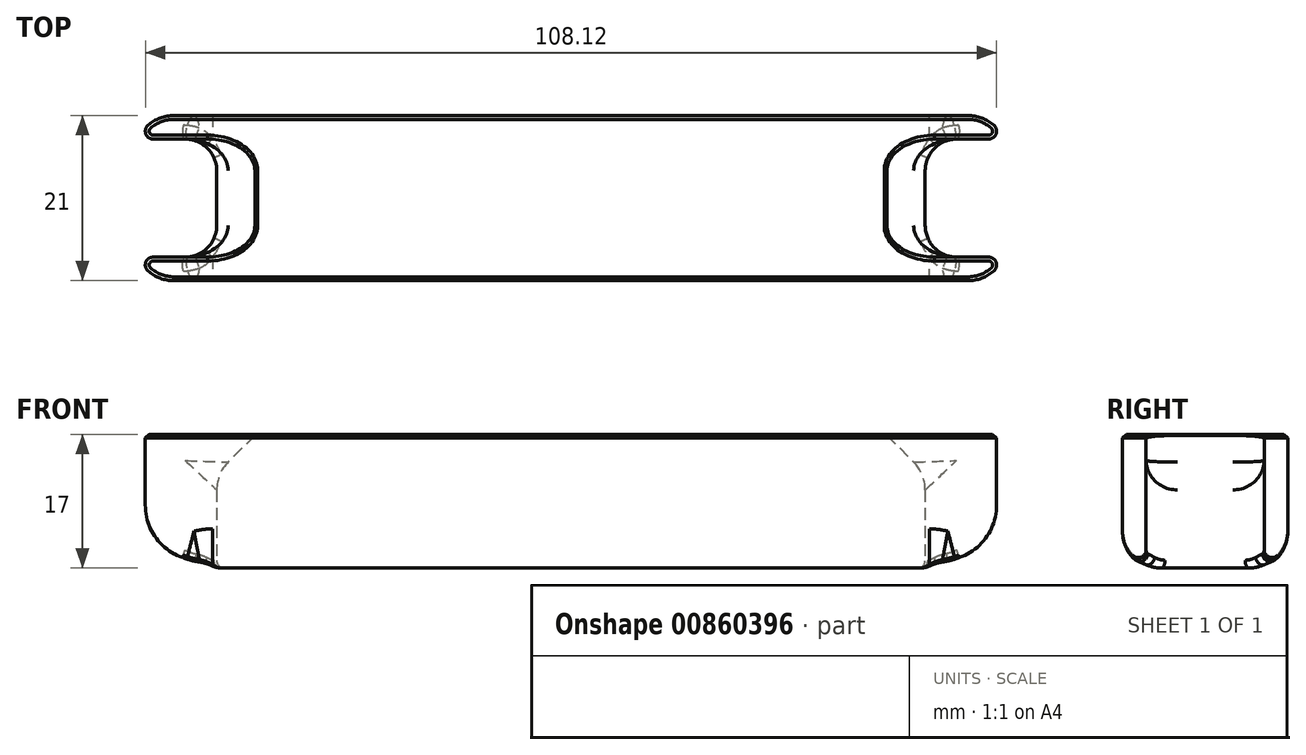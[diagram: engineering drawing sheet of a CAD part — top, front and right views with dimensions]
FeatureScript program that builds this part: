
annotation { "Feature Type Name" : "Feature", "Feature Type Description" : "" }
export const myFeature = defineFeature(function(context is Context, id is Id, definition is map)
    precondition{}
    {
        {
            var Q0;
            Q0=qCreatedBy(makeId("Top.planeOp"),FACE);
            var sketch = newSketch(context, id + "F0", { "sketchPlane" : qUnion([Q0])});
            skLineSegment(sketch, "E0.bottom", {"start": v(55, -10.5) * mm, "end": v(-55, -10.5) * mm});
            skLineSegment(sketch, "E0.top", {"start": v(55, 10.5) * mm, "end": v(-55, 10.5) * mm});
            skLineSegment(sketch, "E0.left", {"start": v(55, -10.5) * mm, "end": v(55, 10.5) * mm});
            skLineSegment(sketch, "E0.right", {"start": v(-55, -10.5) * mm, "end": v(-55, 10.5) * mm});
            skPoint(sketch, "E0.middle", {"position": v(0, 0) * mm});
            skLineSegment(sketch, "E1.bottom", {"start": v(-55, 7.5) * mm, "end": v(-45, 7.5) * mm});
            skLineSegment(sketch, "E1.top", {"start": v(-55, -7.5) * mm, "end": v(-45, -7.5) * mm});
            skLineSegment(sketch, "E1.left", {"start": v(-55, 7.5) * mm, "end": v(-55, -7.5) * mm});
            skLineSegment(sketch, "E1.right", {"start": v(-45, 7.5) * mm, "end": v(-45, -7.5) * mm});
            skLineSegment(sketch, "E2.bottom", {"start": v(55, 7.5) * mm, "end": v(45, 7.5) * mm});
            skLineSegment(sketch, "E2.top", {"start": v(55, -7.5) * mm, "end": v(45, -7.5) * mm});
            skLineSegment(sketch, "E2.left", {"start": v(55, 7.5) * mm, "end": v(55, -7.5) * mm});
            skLineSegment(sketch, "E2.right", {"start": v(45, 7.5) * mm, "end": v(45, -7.5) * mm});
            skSolve(sketch);
        }
        {
            var Q0;
            {var subQ6=sQuery(id+"F0.wireOp",EDGE,"E0.bottom");Q0=makeQuery(id+"F0.imprint","IMPRINT",FACE,{"disambiguationData":[TD([[makeQuery(id+"F0.imprint","IMPRINT",EDGE,{"derivedFrom":subQ6}),-1.0]])]});}
            extrude(context, id + "F1", {"entities" : qUnion([Q0]), "depth" : 17 * mm, "offsetDistance" : 25 * mm});
        }
        {
            var Q0;
            Q0=makeQuery(id+"F1.opExtrude","CAP_EDGE",EDGE,{"disambiguationData":[OSD([sQuery(id+"F0.wireOp",EDGE,"E1.right")])],"isStart":false});
            var Q1;
            Q1=makeQuery(id+"F1.opExtrude","CAP_EDGE",EDGE,{"disambiguationData":[OSD([sQuery(id+"F0.wireOp",EDGE,"E2.right")])],"isStart":false});
            chamfer(context, id + "F2", {"entities" : qUnion([Q0, Q1]), "width" : 5 * mm, "tangentPropagation" : true});
        }
        {
            var Q0;
            Q0=makeQuery(id+"F1.opExtrude","SWEPT_EDGE",EDGE,{"disambiguationData":[OSD([sQuery(id+"F0.wireOp",EDGE,"E2.bottom"),sQuery(id+"F0.wireOp",EDGE,"E2.right")])]});
            var Q1;
            Q1=makeQuery(id+"F1.opExtrude","SWEPT_EDGE",EDGE,{"disambiguationData":[OSD([sQuery(id+"F0.wireOp",EDGE,"E2.top"),sQuery(id+"F0.wireOp",EDGE,"E2.right")])]});
            var Q2;
            Q2=makeQuery(id+"F1.opExtrude","SWEPT_EDGE",EDGE,{"disambiguationData":[OSD([sQuery(id+"F0.wireOp",EDGE,"E1.top"),sQuery(id+"F0.wireOp",EDGE,"E1.right")])]});
            var Q3;
            Q3=makeQuery(id+"F1.opExtrude","SWEPT_EDGE",EDGE,{"disambiguationData":[OSD([sQuery(id+"F0.wireOp",EDGE,"E1.bottom"),sQuery(id+"F0.wireOp",EDGE,"E1.right")])]});
            var Q4;
            Q4=makeQuery(id+"F2.opChamfer","BLEND_EDGE",EDGE,{"blendedFrom":[makeQuery(id+"F1.opExtrude","CAP_EDGE",EDGE,{"disambiguationData":[OSD([sQuery(id+"F0.wireOp",EDGE,"E1.right")])],"isStart":false}),makeQuery(id+"F1.opExtrude","SWEPT_FACE",FACE,{"disambiguationData":[OSD([sQuery(id+"F0.wireOp",EDGE,"E1.top")])]})],"blendedInto":[makeQuery(id+"F1.opExtrude","SWEPT_FACE",FACE,{"disambiguationData":[OSD([sQuery(id+"F0.wireOp",EDGE,"E1.top")])]})]});
            var Q5;
            Q5=makeQuery(id+"F2.opChamfer","BLEND_EDGE",EDGE,{"blendedFrom":[makeQuery(id+"F1.opExtrude","CAP_EDGE",EDGE,{"disambiguationData":[OSD([sQuery(id+"F0.wireOp",EDGE,"E1.right")])],"isStart":false}),makeQuery(id+"F1.opExtrude","SWEPT_FACE",FACE,{"disambiguationData":[OSD([sQuery(id+"F0.wireOp",EDGE,"E1.bottom")])]})],"blendedInto":[makeQuery(id+"F1.opExtrude","SWEPT_FACE",FACE,{"disambiguationData":[OSD([sQuery(id+"F0.wireOp",EDGE,"E1.bottom")])]})]});
            var Q6;
            Q6=makeQuery(id+"F2.opChamfer","BLEND_EDGE",EDGE,{"blendedFrom":[makeQuery(id+"F1.opExtrude","CAP_EDGE",EDGE,{"disambiguationData":[OSD([sQuery(id+"F0.wireOp",EDGE,"E2.right")])],"isStart":false}),makeQuery(id+"F1.opExtrude","SWEPT_FACE",FACE,{"disambiguationData":[OSD([sQuery(id+"F0.wireOp",EDGE,"E2.bottom")])]})],"blendedInto":[makeQuery(id+"F1.opExtrude","SWEPT_FACE",FACE,{"disambiguationData":[OSD([sQuery(id+"F0.wireOp",EDGE,"E2.bottom")])]})]});
            var Q7;
            Q7=makeQuery(id+"F2.opChamfer","BLEND_EDGE",EDGE,{"blendedFrom":[makeQuery(id+"F1.opExtrude","CAP_EDGE",EDGE,{"disambiguationData":[OSD([sQuery(id+"F0.wireOp",EDGE,"E2.right")])],"isStart":false}),makeQuery(id+"F1.opExtrude","SWEPT_FACE",FACE,{"disambiguationData":[OSD([sQuery(id+"F0.wireOp",EDGE,"E2.top")])]})],"blendedInto":[makeQuery(id+"F1.opExtrude","SWEPT_FACE",FACE,{"disambiguationData":[OSD([sQuery(id+"F0.wireOp",EDGE,"E2.top")])]})]});
            fillet(context, id + "F3", {"entities" : qUnion([Q0, Q1, Q2, Q3, Q4, Q5, Q6, Q7]), "radius" : 4 * mm, "tangentPropagation" : true, "allowEdgeOverflow" : false});
        }
        {
            var Q0;
            {var subQ0=sQuery(id+"F0.wireOp",EDGE,"E0.right");Q0=makeQuery(id+"F1.opExtrude","CAP_EDGE",EDGE,{"disambiguationData":[OSD([subQ0]),TDD([makeQuery(id+"F0.imprint","IMPRINT",EDGE,{"disambiguationData":[TD([[makeQuery(id+"F0.imprint","INTERSECT",VERTEX,{"derivedFrom":[sQuery(id+"F0.wireOp",EDGE,"E0.top"),subQ0]}),1.0]])],"derivedFrom":subQ0})])],"isStart":true});}
            var Q1;
            {var subQ0=sQuery(id+"F0.wireOp",EDGE,"E0.left");Q1=makeQuery(id+"F1.opExtrude","CAP_EDGE",EDGE,{"disambiguationData":[OSD([subQ0]),TDD([makeQuery(id+"F0.imprint","IMPRINT",EDGE,{"disambiguationData":[TD([[makeQuery(id+"F0.imprint","INTERSECT",VERTEX,{"derivedFrom":[sQuery(id+"F0.wireOp",EDGE,"E0.top"),subQ0]}),1.0]])],"derivedFrom":subQ0})])],"isStart":true});}
            var Q2;
            {var subQ0=sQuery(id+"F0.wireOp",EDGE,"E0.left");Q2=makeQuery(id+"F1.opExtrude","CAP_EDGE",EDGE,{"disambiguationData":[OSD([subQ0]),TDD([makeQuery(id+"F0.imprint","IMPRINT",EDGE,{"disambiguationData":[TD([[makeQuery(id+"F0.imprint","INTERSECT",VERTEX,{"derivedFrom":[sQuery(id+"F0.wireOp",EDGE,"E0.bottom"),subQ0]}),-1.0]])],"derivedFrom":subQ0})])],"isStart":true});}
            var Q3;
            {var subQ0=sQuery(id+"F0.wireOp",EDGE,"E0.right");Q3=makeQuery(id+"F1.opExtrude","CAP_EDGE",EDGE,{"disambiguationData":[OSD([subQ0]),TDD([makeQuery(id+"F0.imprint","IMPRINT",EDGE,{"disambiguationData":[TD([[makeQuery(id+"F0.imprint","INTERSECT",VERTEX,{"derivedFrom":[sQuery(id+"F0.wireOp",EDGE,"E0.bottom"),subQ0]}),-1.0]])],"derivedFrom":subQ0})])],"isStart":true});}
            fillet(context, id + "F4", {"entities" : qUnion([Q0, Q1, Q2, Q3]), "radius" : 8 * mm, "tangentPropagation" : true, "allowEdgeOverflow" : false});
        }
        {
            var Q0;
            Q0=makeQuery(id+"F1.opExtrude","CAP_EDGE",EDGE,{"disambiguationData":[OSD([sQuery(id+"F0.wireOp",EDGE,"E0.top")])],"isStart":true});
            var Q1;
            Q1=makeQuery(id+"F1.opExtrude","CAP_EDGE",EDGE,{"disambiguationData":[OSD([sQuery(id+"F0.wireOp",EDGE,"E0.bottom")])],"isStart":true});
            fillet(context, id + "F5", {"entities" : qUnion([Q0, Q1]), "radius" : 5 * mm, "tangentPropagation" : true, "allowEdgeOverflow" : false});
        }
        {
            var Q0;
            {var subQ0=sQuery(id+"F0.wireOp",EDGE,"E1.right");Q0=makeQuery(id+"F2.opChamfer","BLEND_EDGE",EDGE,{"blendedFrom":[makeQuery(id+"F1.opExtrude","CAP_EDGE",EDGE,{"disambiguationData":[OSD([subQ0])],"isStart":false}),makeQuery(id+"F1.opExtrude","SWEPT_FACE",FACE,{"disambiguationData":[OSD([subQ0])]})],"blendedInto":[makeQuery(id+"F1.opExtrude","SWEPT_FACE",FACE,{"disambiguationData":[OSD([subQ0])]})]});}
            var Q1;
            {var subQ0=sQuery(id+"F0.wireOp",EDGE,"E2.right");Q1=makeQuery(id+"F2.opChamfer","BLEND_EDGE",EDGE,{"blendedFrom":[makeQuery(id+"F1.opExtrude","CAP_EDGE",EDGE,{"disambiguationData":[OSD([subQ0])],"isStart":false}),makeQuery(id+"F1.opExtrude","SWEPT_FACE",FACE,{"disambiguationData":[OSD([subQ0])]})],"blendedInto":[makeQuery(id+"F1.opExtrude","SWEPT_FACE",FACE,{"disambiguationData":[OSD([subQ0])]})]});}
            fillet(context, id + "F6", {"entities" : qUnion([Q0, Q1]), "radius" : 5 * mm, "tangentPropagation" : true, "allowEdgeOverflow" : false});
        }
        {
            var Q0;
            Q0=makeQuery(id+"F5.opFillet","BLEND_EDGE",EDGE,{"blendedFrom":[makeQuery(id+"F1.opExtrude","CAP_EDGE",EDGE,{"disambiguationData":[OSD([sQuery(id+"F0.wireOp",EDGE,"E0.bottom")])],"isStart":true}),makeQuery(id+"F1.opExtrude","SWEPT_FACE",FACE,{"disambiguationData":[OSD([sQuery(id+"F0.wireOp",EDGE,"E1.top")])]})],"blendedInto":[makeQuery(id+"F1.opExtrude","SWEPT_FACE",FACE,{"disambiguationData":[OSD([sQuery(id+"F0.wireOp",EDGE,"E1.top")])]})]});
            var Q1;
            Q1=makeQuery(id+"F5.opFillet","BLEND_EDGE",EDGE,{"blendedFrom":[makeQuery(id+"F1.opExtrude","CAP_EDGE",EDGE,{"disambiguationData":[OSD([sQuery(id+"F0.wireOp",EDGE,"E0.top")])],"isStart":true}),makeQuery(id+"F1.opExtrude","SWEPT_FACE",FACE,{"disambiguationData":[OSD([sQuery(id+"F0.wireOp",EDGE,"E2.bottom")])]})],"blendedInto":[makeQuery(id+"F1.opExtrude","SWEPT_FACE",FACE,{"disambiguationData":[OSD([sQuery(id+"F0.wireOp",EDGE,"E2.bottom")])]})]});
            fillet(context, id + "F7", {"entities" : qUnion([Q0, Q1]), "radius" : 1 * mm, "tangentPropagation" : true, "allowEdgeOverflow" : false});
        }
        {
            var Q0;
            Q0=makeQuery(id+"F1.opExtrude","CAP_EDGE",EDGE,{"disambiguationData":[OSD([sQuery(id+"F0.wireOp",EDGE,"E0.bottom")])],"isStart":false});
            chamfer(context, id + "F8", {"entities" : qUnion([Q0]), "width" : 0.5 * mm, "tangentPropagation" : true});
        }
    });
